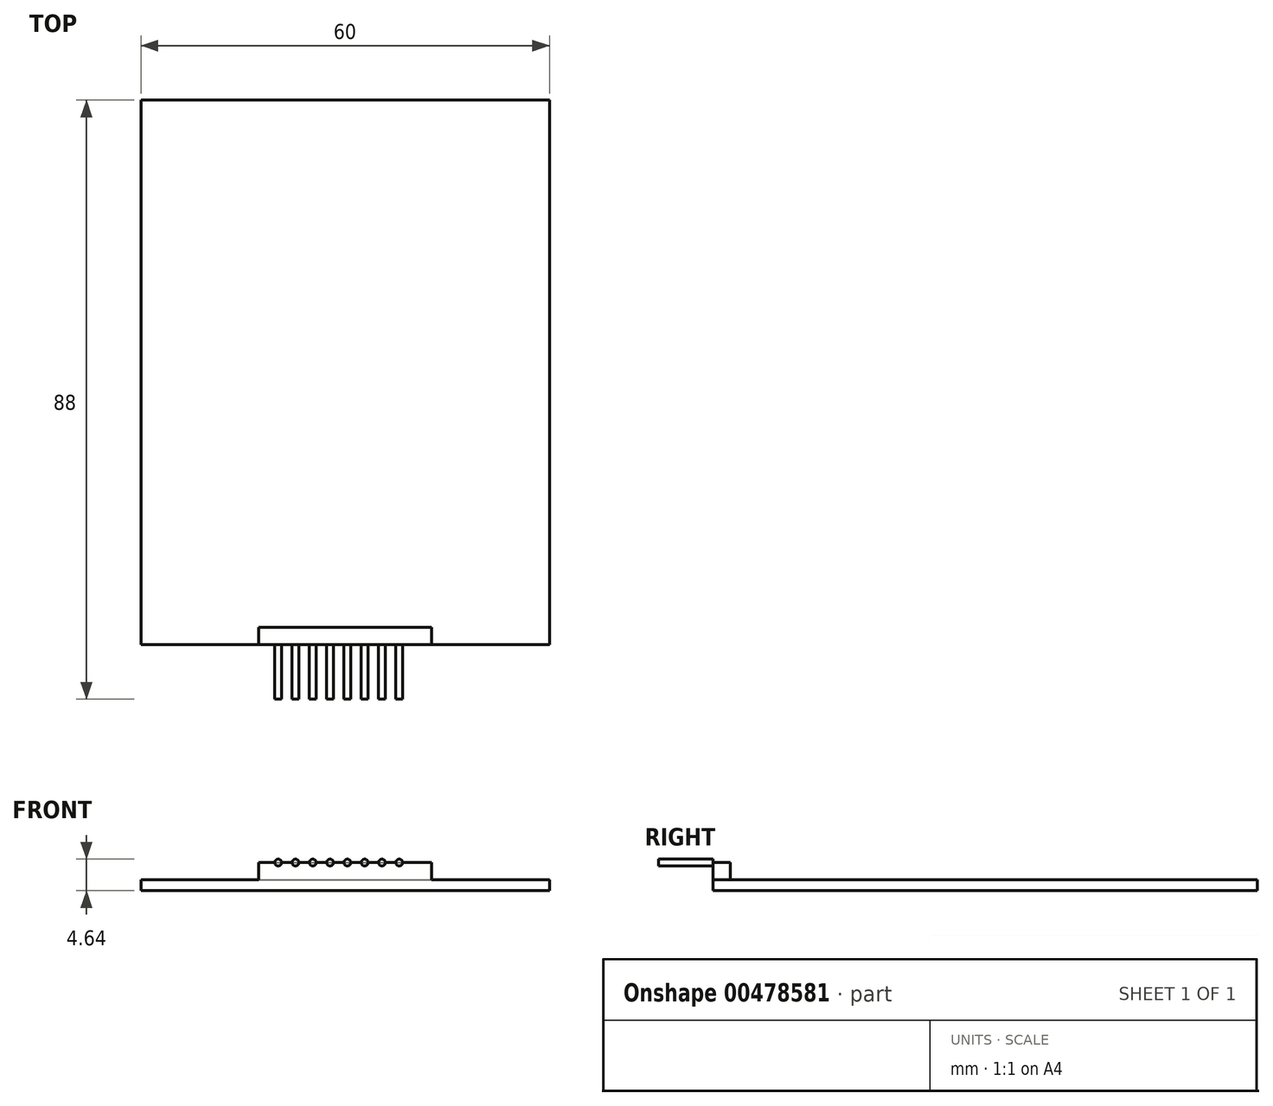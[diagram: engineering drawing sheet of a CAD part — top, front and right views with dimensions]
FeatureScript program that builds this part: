
annotation { "Feature Type Name" : "Feature", "Feature Type Description" : "" }
export const myFeature = defineFeature(function(context is Context, id is Id, definition is map)
    precondition{}
    {
        {
            var Q0;
            Q0=qCreatedBy(makeId("Top.planeOp"),FACE);
            var sketch = newSketch(context, id + "F0", { "sketchPlane" : qUnion([Q0])});
            skLineSegment(sketch, "E0.bottom", {"start": v(0, 0) * mm, "end": v(60, 0) * mm});
            skLineSegment(sketch, "E0.top", {"start": v(0, 80) * mm, "end": v(60, 80) * mm});
            skLineSegment(sketch, "E0.left", {"start": v(0, 0) * mm, "end": v(0, 80) * mm});
            skLineSegment(sketch, "E0.right", {"start": v(60, 0) * mm, "end": v(60, 80) * mm});
            skSolve(sketch);
        }
        {
            var Q0;
            Q0 = qSketchRegion(id + "F0", true);
            extrude(context, id + "F1", {"entities" : qUnion([Q0]), "depth" : 1.6 * mm});
        }
        {
            var Q0;
            Q0=makeQuery(id+"F1.opExtrude","CAP_FACE",FACE,{"disambiguationData":[OSD([sQuery(id+"F0.wireOp",EDGE,"E0.bottom"),sQuery(id+"F0.wireOp",EDGE,"E0.top"),sQuery(id+"F0.wireOp",EDGE,"E0.left"),sQuery(id+"F0.wireOp",EDGE,"E0.right")])],"isStart":false});
            var sketch = newSketch(context, id + "F2", { "sketchPlane" : qUnion([Q0])});
            skLineSegment(sketch, "E1.bottom", {"start": v(17.3, 0) * mm, "end": v(42.7, 0) * mm});
            skLineSegment(sketch, "E1.top", {"start": v(17.3, 2.54) * mm, "end": v(42.7, 2.54) * mm});
            skLineSegment(sketch, "E1.left", {"start": v(17.3, 0) * mm, "end": v(17.3, 2.54) * mm});
            skLineSegment(sketch, "E1.right", {"start": v(42.7, 0) * mm, "end": v(42.7, 2.54) * mm});
            skLineSegment(sketch, "E2", {"start": v(30, 2.54) * mm, "end": v(30, 0) * mm, "construction": true});
            skSolve(sketch);
        }
        {
            var Q0;
            Q0 = qSketchRegion(id + "F2", true);
            extrude(context, id + "F3", {"entities" : qUnion([Q0]), "operationType" : NewBodyOperationType.ADD, "depth" : 2.54 * mm});
        }
        {
            var Q0;
            Q0=makeQuery(id+"F3.boolean.opBoolean","MERGE",FACE,{"derivedFrom":[makeQuery(id+"F1.opExtrude","SWEPT_FACE",FACE,{"disambiguationData":[OSD([sQuery(id+"F0.wireOp",EDGE,"E0.bottom")])]}),makeQuery(id+"F3.opExtrude","SWEPT_FACE",FACE,{"disambiguationData":[OSD([sQuery(id+"F2.wireOp",EDGE,"E1.bottom")])]})]});
            var sketch = newSketch(context, id + "F4", { "sketchPlane" : qUnion([Q0])});
            skCircle(sketch, "E3", {"center": v(20.16, 4.14) * mm, "radius": 0.5 * mm});
            skCircle(sketch, "E4.1.0.0", {"center": v(22.7, 4.14) * mm, "radius": 0.5 * mm});
            skCircle(sketch, "E4.2.0.0", {"center": v(25.24, 4.14) * mm, "radius": 0.5 * mm});
            skCircle(sketch, "E4.3.0.0", {"center": v(27.78, 4.14) * mm, "radius": 0.5 * mm});
            skCircle(sketch, "E4.4.0.0", {"center": v(30.32, 4.14) * mm, "radius": 0.5 * mm});
            skCircle(sketch, "E4.5.0.0", {"center": v(32.86, 4.14) * mm, "radius": 0.5 * mm});
            skCircle(sketch, "E4.6.0.0", {"center": v(35.4, 4.14) * mm, "radius": 0.5 * mm});
            skCircle(sketch, "E4.7.0.0", {"center": v(37.94, 4.14) * mm, "radius": 0.5 * mm});
            skLineSegment(sketch, "E4.direction1", {"start": v(20.16, 4.14) * mm, "end": v(22.7, 4.14) * mm, "construction": true});
            skSolve(sketch);
        }
        {
            var Q0;
            Q0 = qSketchRegion(id + "F4", true);
            extrude(context, id + "F5", {"entities" : qUnion([Q0]), "operationType" : NewBodyOperationType.ADD, "depth" : 8 * mm});
        }
    });
